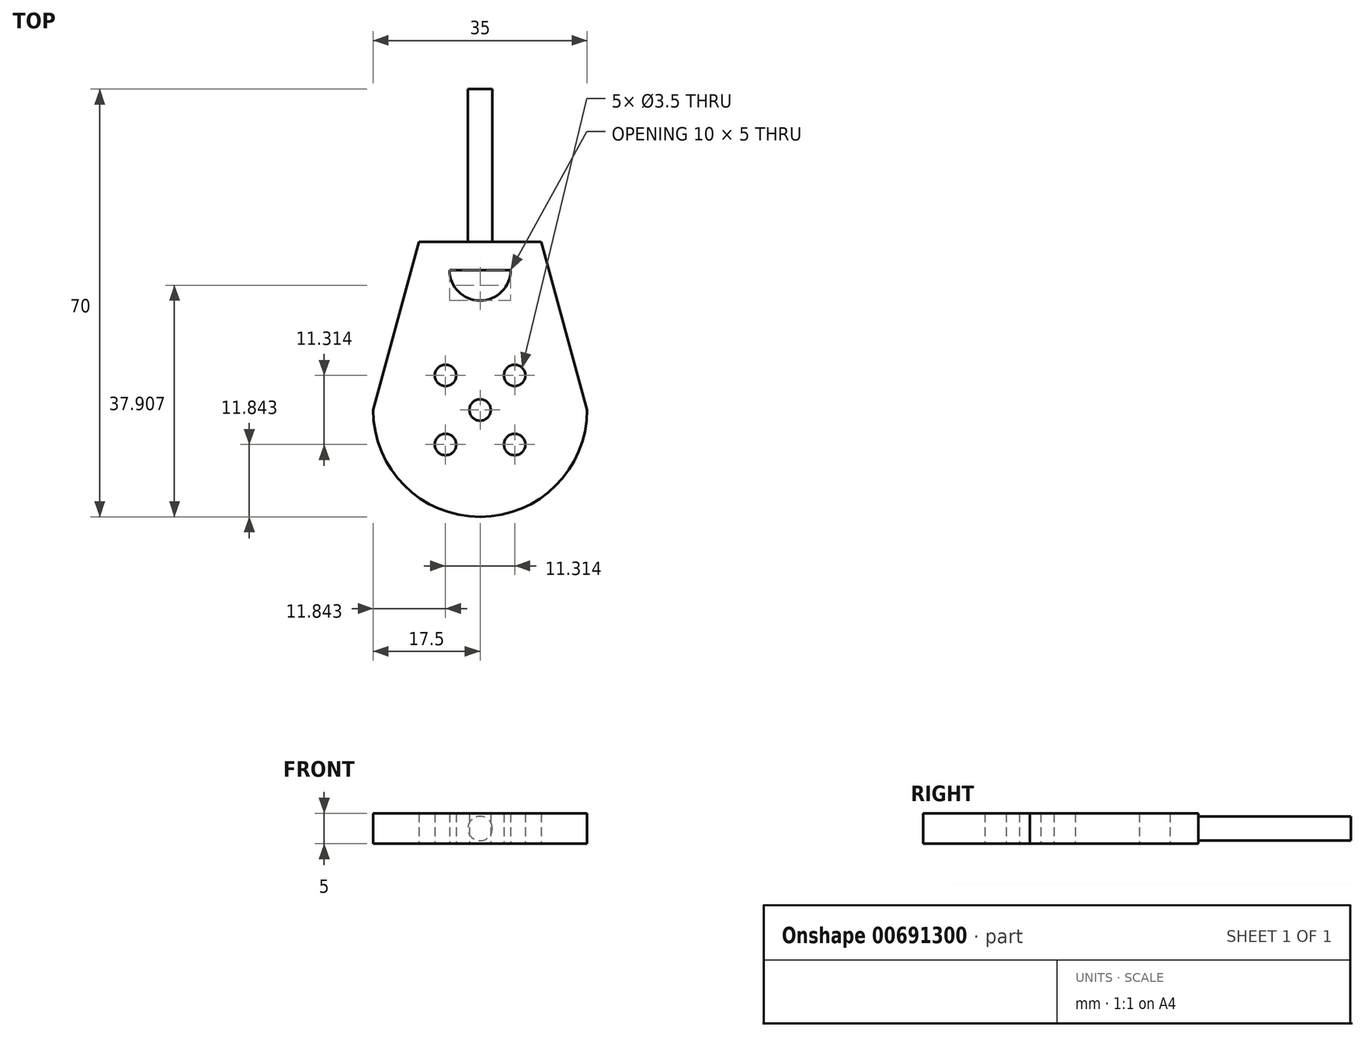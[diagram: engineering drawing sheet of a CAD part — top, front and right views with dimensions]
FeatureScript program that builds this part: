
annotation { "Feature Type Name" : "Feature", "Feature Type Description" : "" }
export const myFeature = defineFeature(function(context is Context, id is Id, definition is map)
    precondition{}
    {
        {
            var Q0;
            Q0=qCreatedBy(makeId("Top.planeOp"),FACE);
            var sketch = newSketch(context, id + "F0", { "sketchPlane" : qUnion([Q0])});
            skArc(sketch, "E0", {"start": v(-17.5, 0) * mm, "mid": v(0, -17.5) * mm, "end": v(17.5, 0) * mm});
            skLineSegment(sketch, "E1", {"start": v(-17.5, 0) * mm, "end": v(-10, 27.5) * mm});
            skLineSegment(sketch, "E2", {"start": v(10, 27.5) * mm, "end": v(17.5, 0) * mm});
            skLineSegment(sketch, "E3", {"start": v(-10, 27.5) * mm, "end": v(0, 27.5) * mm});
            skLineSegment(sketch, "E4", {"start": v(0, 27.5) * mm, "end": v(10, 27.5) * mm});
            skCircle(sketch, "E5", {"center": v(0, 0) * mm, "radius": 1.75 * mm});
            skCircle(sketch, "E6", {"center": v(5.66, 5.66) * mm, "radius": 1.75 * mm});
            skCircle(sketch, "E7.1.0", {"center": v(-5.66, 5.66) * mm, "radius": 1.75 * mm});
            skCircle(sketch, "E7.2.0", {"center": v(-5.66, -5.66) * mm, "radius": 1.75 * mm});
            skCircle(sketch, "E7.3.0", {"center": v(5.66, -5.66) * mm, "radius": 1.75 * mm});
            skLineSegment(sketch, "E8", {"start": v(0, 22.9) * mm, "end": v(5, 22.9) * mm});
            skLineSegment(sketch, "E9", {"start": v(0, 22.9) * mm, "end": v(-5, 22.9) * mm});
            skArc(sketch, "E10", {"start": v(-5, 22.9) * mm, "mid": v(0, 17.9) * mm, "end": v(5, 22.9) * mm});
            skSolve(sketch);
        }
        {
            var Q0;
            Q0=makeQuery(id+"F0.imprint","IMPRINT",FACE,{"disambiguationData":[TD([[makeQuery(id+"F0.imprint","IMPRINT",EDGE,{"derivedFrom":sQuery(id+"F0.wireOp",EDGE,"E0")}),1.0]])]});
            extrude(context, id + "F1", {"entities" : qUnion([Q0]), "depth" : 5 * mm, "offsetDistance" : 25 * mm});
        }
        {
            var Q0;
            Q0=makeQuery(id+"F1.opExtrude","SWEPT_FACE",FACE,{"disambiguationData":[OSD([sQuery(id+"F0.wireOp",EDGE,"E3"),sQuery(id+"F0.wireOp",EDGE,"E4")])]});
            var sketch = newSketch(context, id + "F2", { "sketchPlane" : qUnion([Q0])});
            skLineSegment(sketch, "E11", {"start": v(0, 0) * mm, "end": v(0, 5.49) * mm});
            skLineSegment(sketch, "E12", {"start": v(10, 2.5) * mm, "end": v(-10, 2.5) * mm});
            skCircle(sketch, "E13", {"center": v(0, 2.5) * mm, "radius": 2 * mm});
            skSolve(sketch);
        }
        {
            var Q0;
            Q0 = qSketchRegion(id + "F2", true);
            extrude(context, id + "F3", {"entities" : qUnion([Q0]), "operationType" : NewBodyOperationType.ADD, "depth" : 25 * mm, "offsetDistance" : 25 * mm});
        }
    });
